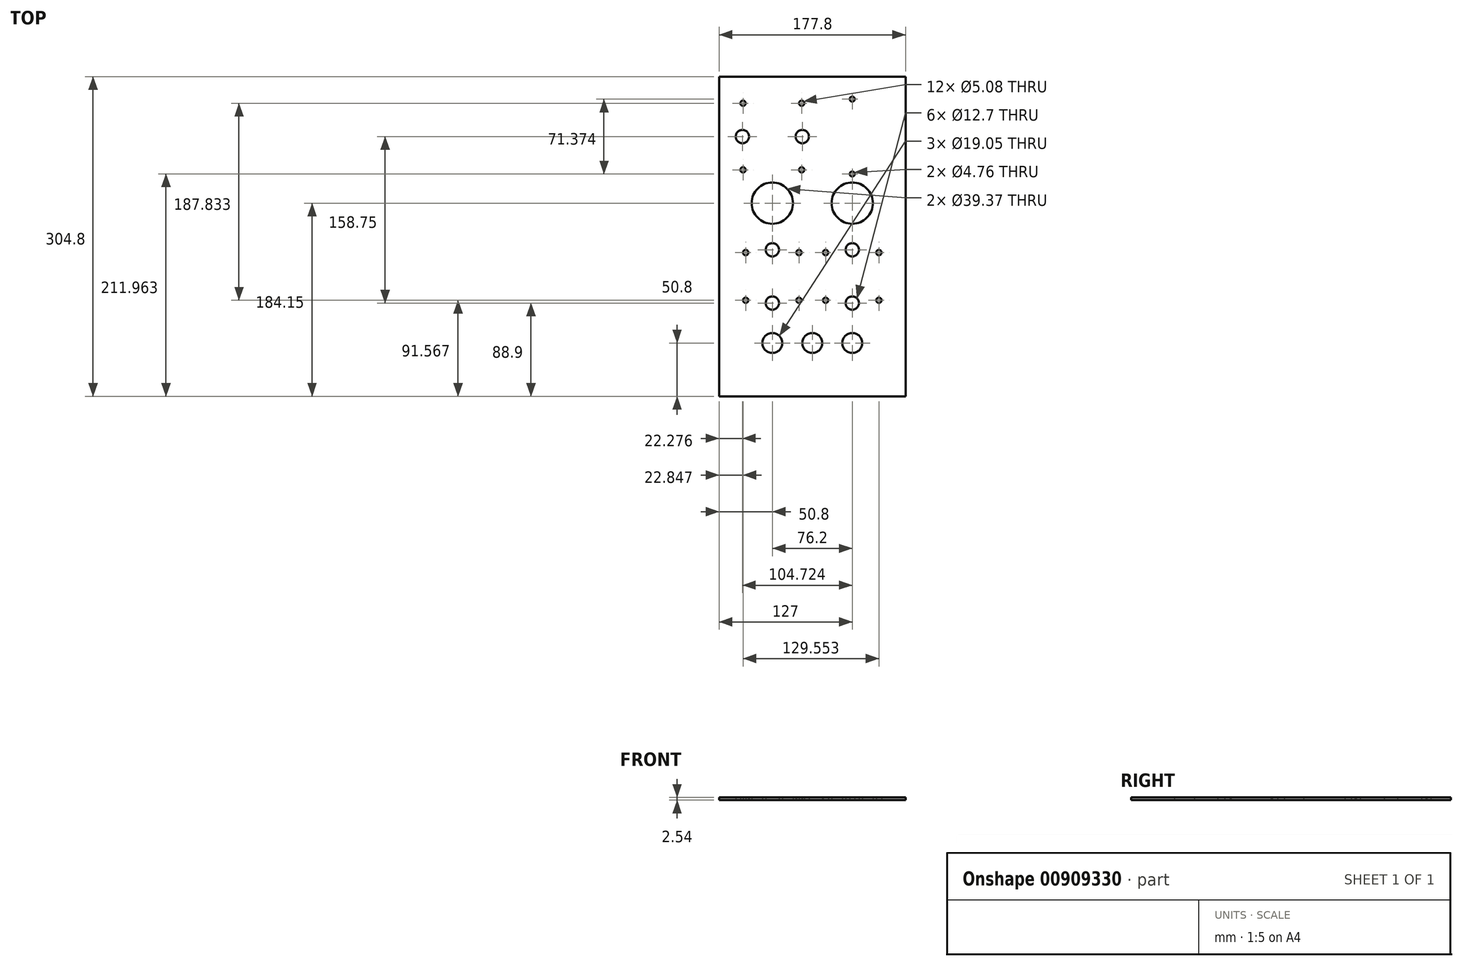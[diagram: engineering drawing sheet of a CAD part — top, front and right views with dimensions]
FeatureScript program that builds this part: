
annotation { "Feature Type Name" : "Feature", "Feature Type Description" : "" }
export const myFeature = defineFeature(function(context is Context, id is Id, definition is map)
    precondition{}
    {
        {
            var Q0;
            Q0=qCreatedBy(makeId("Top.planeOp"),FACE);
            var sketch = newSketch(context, id + "F0", { "sketchPlane" : qUnion([Q0])});
            skLineSegment(sketch, "E0.bottom", {"start": v(0, 0) * mm, "end": v(177.8, 0) * mm});
            skLineSegment(sketch, "E0.top", {"start": v(0, -304.8) * mm, "end": v(177.8, -304.8) * mm});
            skLineSegment(sketch, "E0.left", {"start": v(0, 0) * mm, "end": v(0, -304.8) * mm});
            skLineSegment(sketch, "E0.right", {"start": v(177.8, 0) * mm, "end": v(177.8, -304.8) * mm});
            skLineSegment(sketch, "E1.bottom", {"start": v(25.4, -167.77) * mm, "end": v(76.2, -167.77) * mm, "construction": true});
            skLineSegment(sketch, "E1.top", {"start": v(25.4, -213.23) * mm, "end": v(76.2, -213.23) * mm, "construction": true});
            skLineSegment(sketch, "E1.left", {"start": v(25.4, -167.77) * mm, "end": v(25.4, -213.23) * mm, "construction": true});
            skLineSegment(sketch, "E1.right", {"start": v(76.2, -167.77) * mm, "end": v(76.2, -213.23) * mm, "construction": true});
            skLineSegment(sketch, "E2.bottom", {"start": v(19.05, -154.94) * mm, "end": v(82.55, -154.94) * mm, "construction": true});
            skLineSegment(sketch, "E2.top", {"start": v(19.05, -226.06) * mm, "end": v(82.55, -226.06) * mm, "construction": true});
            skLineSegment(sketch, "E2.left", {"start": v(19.05, -154.94) * mm, "end": v(19.05, -226.06) * mm, "construction": true});
            skLineSegment(sketch, "E2.right", {"start": v(82.55, -154.94) * mm, "end": v(82.55, -226.06) * mm, "construction": true});
            skLineSegment(sketch, "E3", {"start": v(50.8, -154.94) * mm, "end": v(50.8, -226.06) * mm, "construction": true});
            skLineSegment(sketch, "E4", {"start": v(88.9, 0) * mm, "end": v(88.9, 45.6) * mm, "construction": true});
            skLineSegment(sketch, "E5", {"start": v(19.05, -190.5) * mm, "end": v(82.55, -190.5) * mm, "construction": true});
            skCircle(sketch, "E6", {"center": v(50.8, -254) * mm, "radius": 9.53 * mm});
            skCircle(sketch, "E7", {"center": v(127, -254) * mm, "radius": 9.53 * mm});
            skCircle(sketch, "E8", {"center": v(88.9, -254) * mm, "radius": 9.53 * mm});
            skLineSegment(sketch, "E9", {"start": v(50.8, -254) * mm, "end": v(127, -254) * mm, "construction": true});
            skCircle(sketch, "E10", {"center": v(25.4, -167.77) * mm, "radius": 2.54 * mm});
            skCircle(sketch, "E11", {"center": v(76.2, -167.77) * mm, "radius": 2.54 * mm});
            skCircle(sketch, "E12", {"center": v(76.2, -213.23) * mm, "radius": 2.54 * mm});
            skCircle(sketch, "E13", {"center": v(25.4, -213.23) * mm, "radius": 2.54 * mm});
            skCircle(sketch, "E14", {"center": v(50.8, -165.1) * mm, "radius": 6.35 * mm});
            skCircle(sketch, "E15.MirrorC", {"center": v(50.8, -215.9) * mm, "radius": 6.35 * mm});
            skCircle(sketch, "E16.MirrorC", {"center": v(152.4, -167.77) * mm, "radius": 2.54 * mm});
            skCircle(sketch, "E17.MirrorC", {"center": v(101.6, -167.77) * mm, "radius": 2.54 * mm});
            skCircle(sketch, "E18.MirrorC", {"center": v(101.6, -213.23) * mm, "radius": 2.54 * mm});
            skCircle(sketch, "E19.MirrorC", {"center": v(152.4, -213.23) * mm, "radius": 2.54 * mm});
            skCircle(sketch, "E20.MirrorC", {"center": v(127, -215.9) * mm, "radius": 6.35 * mm});
            skCircle(sketch, "E21.MirrorC", {"center": v(127, -165.1) * mm, "radius": 6.35 * mm});
            skLineSegment(sketch, "E22.MirrorCS", {"start": v(127, -154.94) * mm, "end": v(127, -226.06) * mm, "construction": true});
            skLineSegment(sketch, "E23.MirrorCS", {"start": v(152.4, -167.77) * mm, "end": v(152.4, -213.23) * mm, "construction": true});
            skLineSegment(sketch, "E24.MirrorCS", {"start": v(152.4, -213.23) * mm, "end": v(101.6, -213.23) * mm, "construction": true});
            skLineSegment(sketch, "E25.MirrorCS", {"start": v(101.6, -167.77) * mm, "end": v(101.6, -213.23) * mm, "construction": true});
            skLineSegment(sketch, "E26.MirrorCS", {"start": v(158.75, -190.5) * mm, "end": v(95.25, -190.5) * mm, "construction": true});
            skLineSegment(sketch, "E27.MirrorCS", {"start": v(158.75, -154.94) * mm, "end": v(95.25, -154.94) * mm, "construction": true});
            skLineSegment(sketch, "E28.MirrorCS", {"start": v(152.4, -167.77) * mm, "end": v(101.6, -167.77) * mm, "construction": true});
            skLineSegment(sketch, "E29.MirrorCS", {"start": v(95.25, -154.94) * mm, "end": v(95.25, -226.06) * mm, "construction": true});
            skLineSegment(sketch, "E30.MirrorCS", {"start": v(158.75, -226.06) * mm, "end": v(95.25, -226.06) * mm, "construction": true});
            skLineSegment(sketch, "E31.MirrorCS", {"start": v(158.75, -154.94) * mm, "end": v(158.75, -226.06) * mm, "construction": true});
            skLineSegment(sketch, "E32.bottom", {"start": v(22.85, -25.4) * mm, "end": v(78.75, -25.4) * mm, "construction": true});
            skLineSegment(sketch, "E32.top", {"start": v(22.85, -88.9) * mm, "end": v(78.75, -88.9) * mm, "construction": true});
            skLineSegment(sketch, "E32.left", {"start": v(22.85, -25.4) * mm, "end": v(22.85, -88.9) * mm, "construction": true});
            skLineSegment(sketch, "E32.right", {"start": v(78.75, -25.4) * mm, "end": v(78.75, -88.9) * mm, "construction": true});
            skLineSegment(sketch, "E33", {"start": v(22.85, -57.15) * mm, "end": v(78.75, -57.15) * mm, "construction": true});
            skCircle(sketch, "E34", {"center": v(22.28, -57.15) * mm, "radius": 6.35 * mm});
            skCircle(sketch, "E35", {"center": v(79.32, -57.15) * mm, "radius": 6.35 * mm});
            skLineSegment(sketch, "E36", {"start": v(50.8, -25.4) * mm, "end": v(50.8, -88.9) * mm, "construction": true});
            skCircle(sketch, "E37", {"center": v(22.85, -25.4) * mm, "radius": 2.54 * mm});
            skCircle(sketch, "E38", {"center": v(78.75, -25.4) * mm, "radius": 2.54 * mm});
            skCircle(sketch, "E39", {"center": v(22.85, -88.9) * mm, "radius": 2.54 * mm});
            skCircle(sketch, "E40", {"center": v(78.75, -88.9) * mm, "radius": 2.54 * mm});
            skCircle(sketch, "E41", {"center": v(127, -21.46) * mm, "radius": 2.38 * mm});
            skCircle(sketch, "E42", {"center": v(127, -92.84) * mm, "radius": 2.38 * mm});
            skLineSegment(sketch, "E43", {"start": v(127, -21.46) * mm, "end": v(127, -92.84) * mm, "construction": true});
            skLineSegment(sketch, "E44.bottom", {"start": v(101.6, -31.75) * mm, "end": v(152.4, -31.75) * mm, "construction": true});
            skLineSegment(sketch, "E44.top", {"start": v(101.6, -82.55) * mm, "end": v(152.4, -82.55) * mm, "construction": true});
            skLineSegment(sketch, "E44.left", {"start": v(101.6, -31.75) * mm, "end": v(101.6, -82.55) * mm, "construction": true});
            skLineSegment(sketch, "E44.right", {"start": v(152.4, -31.75) * mm, "end": v(152.4, -82.55) * mm, "construction": true});
            skCircle(sketch, "E45", {"center": v(127, -120.65) * mm, "radius": 19.69 * mm});
            skCircle(sketch, "E46", {"center": v(50.8, -120.65) * mm, "radius": 19.69 * mm});
            skSolve(sketch);
        }
        {
            var Q0;
            Q0=makeQuery(id+"F0.imprint","IMPRINT",FACE,{"disambiguationData":[TD([[makeQuery(id+"F0.imprint","IMPRINT",EDGE,{"derivedFrom":sQuery(id+"F0.wireOp",EDGE,"E0.bottom")}),-1.0]])]});
            extrude(context, id + "F1", {"entities" : qUnion([Q0]), "depth" : 2.54 * mm});
        }
    });
